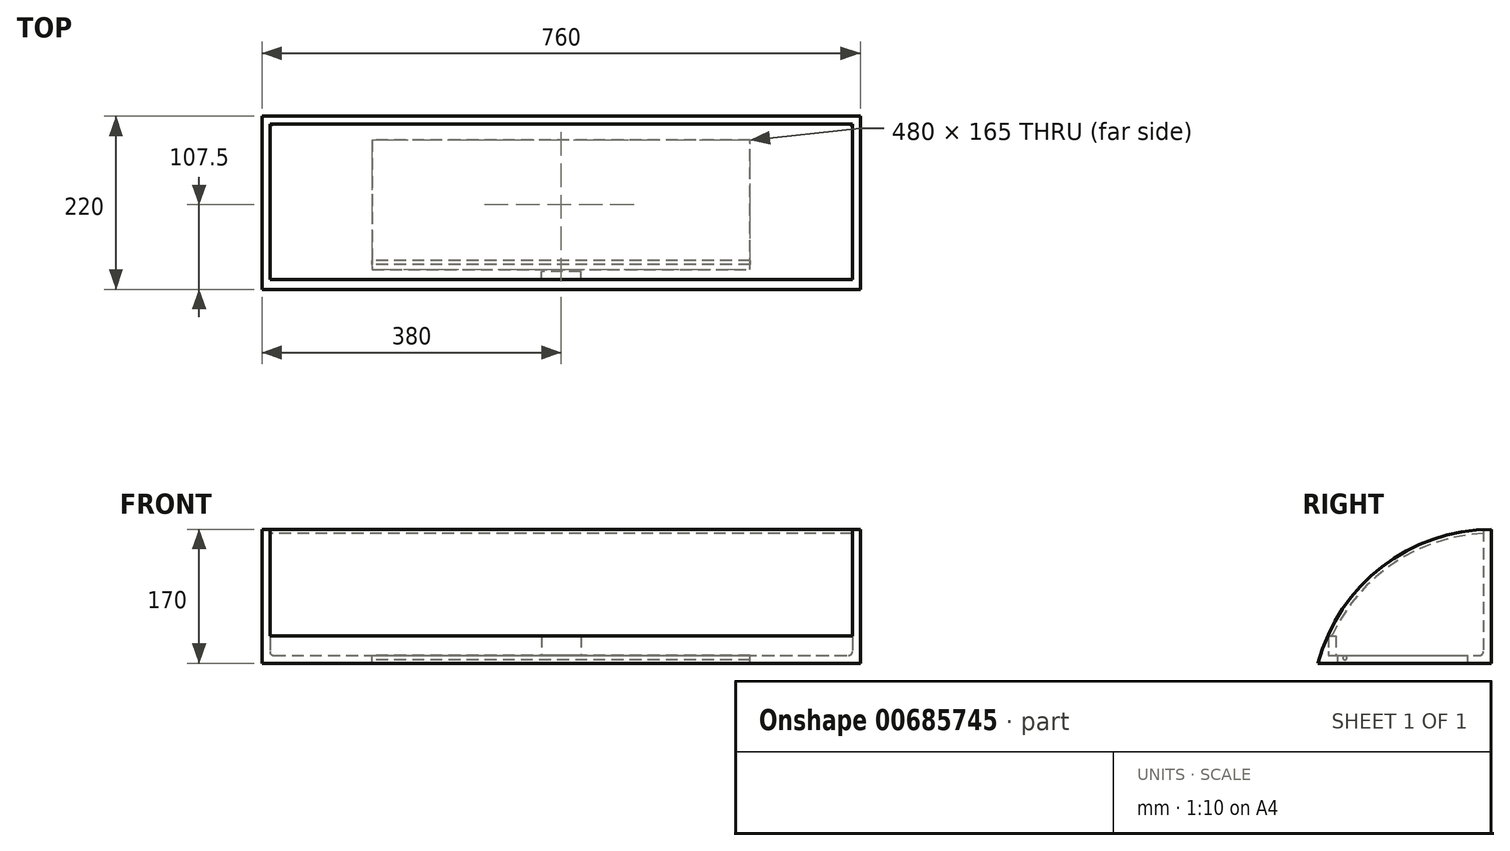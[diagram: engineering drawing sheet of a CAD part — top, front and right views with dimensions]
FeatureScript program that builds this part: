
annotation { "Feature Type Name" : "Feature", "Feature Type Description" : "" }
export const myFeature = defineFeature(function(context is Context, id is Id, definition is map)
    precondition{}
    {
        {
            var Q0;
            Q0=qCreatedBy(makeId("Top.planeOp"),FACE);
            var sketch = newSketch(context, id + "F0", { "sketchPlane" : qUnion([Q0])});
            skLineSegment(sketch, "E0.bottom", {"start": v(0, 0) * mm, "end": v(760, 0) * mm});
            skLineSegment(sketch, "E0.top", {"start": v(0, 220) * mm, "end": v(760, 220) * mm});
            skLineSegment(sketch, "E0.left", {"start": v(0, 0) * mm, "end": v(0, 220) * mm});
            skLineSegment(sketch, "E0.right", {"start": v(760, 0) * mm, "end": v(760, 220) * mm});
            skSolve(sketch);
        }
        {
            var Q0;
            Q0=qSketchRegion(id+"F0",true);
            extrude(context, id + "F1", {"entities" : qUnion([Q0]), "depth" : 170 * mm, "offsetDistance" : 25 * mm});
        }
        {
            var Q0;
            Q0=makeQuery(id+"F1.opExtrude","SWEPT_FACE",FACE,{"disambiguationData":[OSD([sQuery(id+"F0.wireOp",EDGE,"E0.left")])]});
            var sketch = newSketch(context, id + "F2", { "sketchPlane" : qUnion([Q0])});
            skArc(sketch, "E1", {"start": v(0, 0) * mm, "mid": v(-80.99, 122.55) * mm, "end": v(-220, 170) * mm});
            skSolve(sketch);
        }
        {
            var Q0;
            Q0=makeQuery(id+"F2.imprint","IMPRINT",FACE,{"disambiguationData":[TD([[makeQuery(id+"F2.imprint","IMPRINT",EDGE,{"derivedFrom":sQuery(id+"F2.wireOp",EDGE,"E1")}),-1.0]])]});
            extrude(context, id + "F3", {"entities" : qUnion([Q0]), "operationType" : NewBodyOperationType.REMOVE, "oppositeDirection" : true, "depth" : 760 * mm, "offsetDistance" : 25 * mm});
        }
        {
            var Q0;
            Q0=makeQuery(id+"F3.boolean.opBoolean","COPY",FACE,{"derivedFrom":makeQuery(id+"F3.opExtrude","SWEPT_FACE",FACE,{"disambiguationData":[OSD([sQuery(id+"F2.wireOp",EDGE,"E1")])]})});
            shell(context, id + "F4", {"entities" : qUnion([Q0]), "thickness" : 10 * mm});
        }
        {
            var Q0;
            Q0=makeQuery(id+"F4.opShell","OFFSET_FACE",FACE,{"disambiguationData":[OSD([sQuery(id+"F0.wireOp",EDGE,"E0.bottom"),sQuery(id+"F0.wireOp",EDGE,"E0.top"),sQuery(id+"F0.wireOp",EDGE,"E0.left"),sQuery(id+"F0.wireOp",EDGE,"E0.right")])]});
            var sketch = newSketch(context, id + "F5", { "sketchPlane" : qUnion([Q0])});
            skLineSegment(sketch, "E2", {"start": v(380, 210) * mm, "end": v(380, 115) * mm});
            skLineSegment(sketch, "E3.bottom", {"start": v(620, 190) * mm, "end": v(140, 190) * mm});
            skLineSegment(sketch, "E3.left", {"start": v(620, 190) * mm, "end": v(620, 40) * mm});
            skLineSegment(sketch, "E3.right", {"start": v(140, 190) * mm, "end": v(140, 40) * mm});
            skPoint(sketch, "E3.middle", {"position": v(380, 115) * mm});
            skLineSegment(sketch, "E4", {"start": v(140, 40) * mm, "end": v(140, 25) * mm});
            skLineSegment(sketch, "E5", {"start": v(140, 25) * mm, "end": v(620, 25) * mm});
            skLineSegment(sketch, "E6", {"start": v(620, 25) * mm, "end": v(620, 40) * mm});
            skSolve(sketch);
        }
        {
            var Q0;
            Q0=qSketchRegion(id+"F5",true);
            extrude(context, id + "F6", {"entities" : qUnion([Q0]), "operationType" : NewBodyOperationType.REMOVE, "oppositeDirection" : true, "depth" : 25 * mm, "offsetDistance" : 25 * mm});
        }
        {
            var Q0;
            Q0=makeQuery(id+"F4.opShell","OFFSET_FACE",FACE,{"disambiguationData":[OSD([sQuery(id+"F0.wireOp",EDGE,"E0.bottom"),sQuery(id+"F0.wireOp",EDGE,"E0.top"),sQuery(id+"F0.wireOp",EDGE,"E0.left"),sQuery(id+"F0.wireOp",EDGE,"E0.right")])]});
            var sketch = newSketch(context, id + "F7", { "sketchPlane" : qUnion([Q0])});
            skLineSegment(sketch, "E7.bottom", {"start": v(10, 2.85) * mm, "end": v(750, 2.85) * mm});
            skLineSegment(sketch, "E7.top", {"start": v(10, 12.85) * mm, "end": v(750, 12.85) * mm});
            skLineSegment(sketch, "E7.left", {"start": v(10, 2.85) * mm, "end": v(10, 12.85) * mm});
            skLineSegment(sketch, "E7.right", {"start": v(750, 2.85) * mm, "end": v(750, 12.85) * mm});
            skLineSegment(sketch, "E8.bottom", {"start": v(405, 2.85) * mm, "end": v(355, 2.85) * mm});
            skLineSegment(sketch, "E8.top", {"start": v(405, 22.85) * mm, "end": v(355, 22.85) * mm});
            skLineSegment(sketch, "E8.left", {"start": v(405, 2.85) * mm, "end": v(405, 22.85) * mm});
            skLineSegment(sketch, "E8.right", {"start": v(355, 2.85) * mm, "end": v(355, 22.85) * mm});
            skPoint(sketch, "E8.middle", {"position": v(380, 12.85) * mm});
            skSolve(sketch);
        }
        {
            var Q0;
            Q0=qSketchRegion(id+"F7",true);
            extrude(context, id + "F8", {"entities" : qUnion([Q0]), "operationType" : NewBodyOperationType.ADD, "depth" : 25 * mm, "offsetDistance" : 25 * mm});
        }
        {
            var Q0;
            Q0=makeQuery(id+"F1.opExtrude","SWEPT_FACE",FACE,{"disambiguationData":[OSD([sQuery(id+"F0.wireOp",EDGE,"E0.left")])]});
            var sketch = newSketch(context, id + "F9", { "sketchPlane" : qUnion([Q0])});
            skLineSegment(sketch, "E9", {"start": v(0, 0) * mm, "end": v(0, 38.46) * mm});
            skLineSegment(sketch, "E10", {"start": v(0, 38.46) * mm, "end": v(-13.82, 38.46) * mm});
            skSolve(sketch);
        }
        {
            var Q0;
            {var subQ0=sQuery(id+"F9.wireOp",EDGE,"E9");Q0=makeQuery(id+"F9.imprint","IMPRINT",FACE,{"disambiguationData":[TD([[makeQuery(id+"F9.imprint","IMPRINT",EDGE,{"derivedFrom":subQ0}),1.0]])]});}
            extrude(context, id + "F10", {"entities" : qUnion([Q0]), "operationType" : NewBodyOperationType.REMOVE, "oppositeDirection" : true, "depth" : 760 * mm, "offsetDistance" : 25 * mm});
        }
        {
            var Q0;
            Q0=makeQuery(id+"F4.opShell","OFFSET_FACE",FACE,{"disambiguationData":[OSD([sQuery(id+"F0.wireOp",EDGE,"E0.left")])]});
            var sketch = newSketch(context, id + "F11", { "sketchPlane" : qUnion([Q0])});
            skArc(sketch, "E11.0", {"start": v(16.82, 32.97) * mm, "mid": v(94.77, 126.38) * mm, "end": v(210.22, 164.78) * mm});
            skLineSegment(sketch, "E12", {"start": v(210.22, 164.78) * mm, "end": v(210, 169.78) * mm});
            skLineSegment(sketch, "E13", {"start": v(16.82, 32.97) * mm, "end": v(12.25, 35) * mm});
            skSolve(sketch);
        }
        {
            var Q0;
            {var subQ0=sQuery(id+"F2.wireOp",EDGE,"E1");var subQ1=sQuery(id+"F0.wireOp",EDGE,"E0.left");var subQ2=makeQuery(id+"F4.opShell","OFFSET_FACE",FACE,{"disambiguationData":[OSD([subQ1])]});var subQ3=makeQuery(id+"F8.boolean.opBoolean","SPLIT",EDGE,{"disambiguationData":[topologyDisambiguationEdgeConnected([subQ2])],"derivedFrom":makeQuery(id+"F4.opShell","OFFSET_EDGE",EDGE,{"disambiguationData":[OSD([subQ0]),TDD([makeQuery(id+"F3.boolean.opBoolean","COPY",EDGE,{"derivedFrom":makeQuery(id+"F3.opExtrude","CAP_EDGE",EDGE,{"disambiguationData":[OSD([subQ0])],"isStart":true})})])]})});Q0=makeQuery(id+"F11.imprint","IMPRINT",FACE,{"disambiguationData":[TD([[makeQuery(id+"F11.imprint","IMPRINT",EDGE,{"derivedFrom":subQ3}),-1.0]])]});}
            extrude(context, id + "F12", {"entities" : qUnion([Q0]), "depth" : 740 * mm, "offsetDistance" : 25 * mm});
        }
        {
            var Q0;
            Q0=makeQuery(id+"F12.opExtrude","SWEPT_EDGE",EDGE,{"disambiguationData":[OSD([sQuery(id+"F11.wireOp",EDGE,"E11.0"),sQuery(id+"F11.wireOp",EDGE,"E13")])]});
            fillet(context, id + "F13", {"entities" : qUnion([Q0]), "radius" : 5 * mm, "tangentPropagation" : true, "allowEdgeOverflow" : false});
        }
        {
            var Q0;
            Q0=makeQuery(id+"F4.opShell","OFFSET_EDGE",EDGE,{"disambiguationData":[OSD([sQuery(id+"F0.wireOp",EDGE,"E0.top"),sQuery(id+"F0.wireOp",EDGE,"E0.left")])]});
            var Q1;
            Q1=makeQuery(id+"F4.opShell","OFFSET_EDGE",EDGE,{"disambiguationData":[OSD([sQuery(id+"F0.wireOp",EDGE,"E0.top"),sQuery(id+"F0.wireOp",EDGE,"E0.right")])]});
            var Q2;
            Q2=makeQuery(id+"F4.opShell","OFFSET_EDGE",EDGE,{"disambiguationData":[OSD([sQuery(id+"F0.wireOp",EDGE,"E0.top")])]});
            var Q3;
            Q3=makeQuery(id+"F4.opShell","OFFSET_EDGE",EDGE,{"disambiguationData":[OSD([sQuery(id+"F0.wireOp",EDGE,"E0.right")])]});
            var Q4;
            Q4=makeQuery(id+"F4.opShell","OFFSET_EDGE",EDGE,{"disambiguationData":[OSD([sQuery(id+"F0.wireOp",EDGE,"E0.left")])]});
            var Q5;
            {var subQ0=sQuery(id+"F7.wireOp",EDGE,"E7.top");Q5=makeQuery(id+"F8.opExtrude","CAP_EDGE",EDGE,{"disambiguationData":[OSD([subQ0]),TDD([makeQuery(id+"F7.imprint","IMPRINT",EDGE,{"disambiguationData":[TD([[makeQuery(id+"F7.imprint","INTERSECT",VERTEX,{"derivedFrom":[subQ0,sQuery(id+"F7.wireOp",EDGE,"E8.right")]}),1.0]])],"derivedFrom":subQ0})])],"isStart":true});}
            var Q6;
            Q6=makeQuery(id+"F8.opExtrude","CAP_EDGE",EDGE,{"disambiguationData":[OSD([sQuery(id+"F7.wireOp",EDGE,"E8.right")])],"isStart":true});
            var Q7;
            Q7=makeQuery(id+"F8.opExtrude","CAP_EDGE",EDGE,{"disambiguationData":[OSD([sQuery(id+"F7.wireOp",EDGE,"E8.top")])],"isStart":true});
            var Q8;
            Q8=makeQuery(id+"F8.opExtrude","CAP_EDGE",EDGE,{"disambiguationData":[OSD([sQuery(id+"F7.wireOp",EDGE,"E8.left")])],"isStart":true});
            var Q9;
            {var subQ0=sQuery(id+"F7.wireOp",EDGE,"E7.top");Q9=makeQuery(id+"F8.opExtrude","CAP_EDGE",EDGE,{"disambiguationData":[OSD([subQ0]),TDD([makeQuery(id+"F7.imprint","IMPRINT",EDGE,{"disambiguationData":[TD([[makeQuery(id+"F7.imprint","INTERSECT",VERTEX,{"derivedFrom":[subQ0,sQuery(id+"F7.wireOp",EDGE,"E8.left")]}),-1.0]])],"derivedFrom":subQ0})])],"isStart":true});}
            fillet(context, id + "F14", {"entities" : qUnion([Q0, Q1, Q2, Q3, Q4, Q5, Q6, Q7, Q8, Q9]), "radius" : 5 * mm, "tangentPropagation" : true, "allowEdgeOverflow" : false});
        }
        {
            var Q0;
            Q0=makeQuery(id+"F6.boolean.opBoolean","COPY",FACE,{"derivedFrom":makeQuery(id+"F6.opExtrude","SWEPT_FACE",FACE,{"disambiguationData":[OSD([sQuery(id+"F5.wireOp",EDGE,"E3.right"),sQuery(id+"F5.wireOp",EDGE,"E4")])]})});
            var sketch = newSketch(context, id + "F15", { "sketchPlane" : qUnion([Q0])});
            skLineSegment(sketch, "E14", {"start": v(25, 7) * mm, "end": v(34, 7) * mm});
            skCircle(sketch, "E15", {"center": v(34, 7) * mm, "radius": 2.5 * mm});
            skSolve(sketch);
        }
        {
            var Q0;
            Q0=qSketchRegion(id+"F15",true);
            extrude(context, id + "F16", {"entities" : qUnion([Q0]), "depth" : 480 * mm, "offsetDistance" : 25 * mm});
        }
    });
